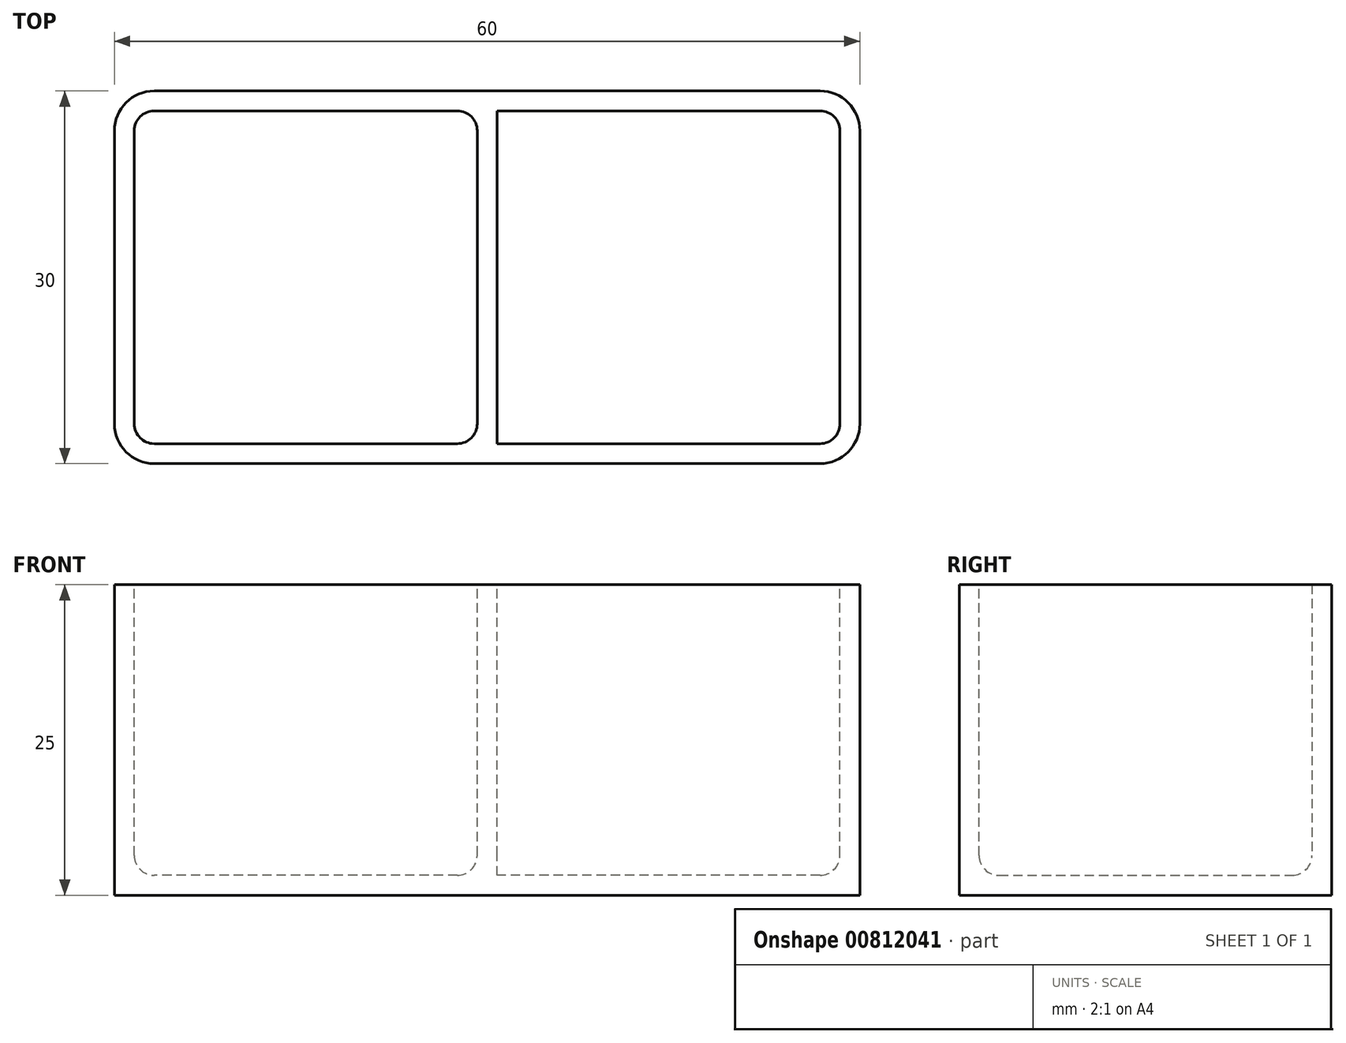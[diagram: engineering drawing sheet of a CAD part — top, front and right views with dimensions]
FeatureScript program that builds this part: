
annotation { "Feature Type Name" : "Feature", "Feature Type Description" : "" }
export const myFeature = defineFeature(function(context is Context, id is Id, definition is map)
    precondition{}
    {
        {
            var Q0;
            Q0=qCreatedBy(makeId("Top.planeOp"),FACE);
            var sketch = newSketch(context, id + "F0", { "sketchPlane" : qUnion([Q0])});
            skLineSegment(sketch, "E0.bottom", {"start": v(30, -15) * mm, "end": v(-30, -15) * mm});
            skLineSegment(sketch, "E0.top", {"start": v(30, 15) * mm, "end": v(-30, 15) * mm});
            skLineSegment(sketch, "E0.left", {"start": v(30, -15) * mm, "end": v(30, 15) * mm});
            skLineSegment(sketch, "E0.right", {"start": v(-30, -15) * mm, "end": v(-30, 15) * mm});
            skPoint(sketch, "E0.middle", {"position": v(0, 0) * mm});
            skSolve(sketch);
        }
        {
            var Q0;
            Q0=makeQuery(id+"F0.imprint","IMPRINT",FACE,{"disambiguationData":[TD([[makeQuery(id+"F0.imprint","IMPRINT",EDGE,{"derivedFrom":sQuery(id+"F0.wireOp",EDGE,"E0.bottom")}),-1.0]])]});
            extrude(context, id + "F1", {"entities" : qUnion([Q0]), "depth" : 25 * mm, "offsetDistance" : 25 * mm});
        }
        {
            var Q0;
            Q0=makeQuery(id+"F1.opExtrude","SWEPT_EDGE",EDGE,{"disambiguationData":[OSD([sQuery(id+"F0.wireOp",EDGE,"E0.top"),sQuery(id+"F0.wireOp",EDGE,"E0.right")])]});
            var Q1;
            Q1=makeQuery(id+"F1.opExtrude","SWEPT_EDGE",EDGE,{"disambiguationData":[OSD([sQuery(id+"F0.wireOp",EDGE,"E0.bottom"),sQuery(id+"F0.wireOp",EDGE,"E0.right")])]});
            var Q2;
            Q2=makeQuery(id+"F1.opExtrude","SWEPT_EDGE",EDGE,{"disambiguationData":[OSD([sQuery(id+"F0.wireOp",EDGE,"E0.bottom"),sQuery(id+"F0.wireOp",EDGE,"E0.left")])]});
            var Q3;
            Q3=makeQuery(id+"F1.opExtrude","SWEPT_EDGE",EDGE,{"disambiguationData":[OSD([sQuery(id+"F0.wireOp",EDGE,"E0.top"),sQuery(id+"F0.wireOp",EDGE,"E0.left")])]});
            fillet(context, id + "F2", {"entities" : qUnion([Q0, Q1, Q2, Q3]), "radius" : 3.2 * mm, "tangentPropagation" : true, "allowEdgeOverflow" : false});
        }
        {
            var Q0;
            Q0=makeQuery(id+"F1.opExtrude","CAP_FACE",FACE,{"disambiguationData":[OSD([sQuery(id+"F0.wireOp",EDGE,"E0.bottom"),sQuery(id+"F0.wireOp",EDGE,"E0.top"),sQuery(id+"F0.wireOp",EDGE,"E0.left"),sQuery(id+"F0.wireOp",EDGE,"E0.right")])],"isStart":false});
            shell(context, id + "F3", {"entities" : qUnion([Q0]), "thickness" : 1.6 * mm});
        }
        {
            var Q0;
            Q0=makeQuery(id+"F1.opExtrude","CAP_FACE",FACE,{"disambiguationData":[OSD([sQuery(id+"F0.wireOp",EDGE,"E0.bottom"),sQuery(id+"F0.wireOp",EDGE,"E0.top"),sQuery(id+"F0.wireOp",EDGE,"E0.left"),sQuery(id+"F0.wireOp",EDGE,"E0.right")])],"isStart":false});
            var sketch = newSketch(context, id + "F4", { "sketchPlane" : qUnion([Q0])});
            skLineSegment(sketch, "E1.0", {"start": v(26.8, 13.4) * mm, "end": v(-26.8, 13.4) * mm});
            skLineSegment(sketch, "E1.1", {"start": v(26.8, -13.4) * mm, "end": v(-26.8, -13.4) * mm});
            skLineSegment(sketch, "E2", {"start": v(0.8, 13.4) * mm, "end": v(0.8, -13.4) * mm});
            skLineSegment(sketch, "E3.MirrorCS", {"start": v(-0.8, 13.4) * mm, "end": v(-0.8, -13.4) * mm});
            skSolve(sketch);
        }
        {
            var Q0;
            {var subQ0=sQuery(id+"F4.wireOp",EDGE,"E2");Q0=makeQuery(id+"F4.imprint","IMPRINT",FACE,{"disambiguationData":[TD([[makeQuery(id+"F4.imprint","IMPRINT",EDGE,{"derivedFrom":subQ0}),-1.0]])]});}
            extrude(context, id + "F5", {"entities" : qUnion([Q0]), "operationType" : NewBodyOperationType.ADD, "endBound" : BoundingType.UP_TO_NEXT, "oppositeDirection" : true, "depth" : 25 * mm, "offsetDistance" : 25 * mm});
        }
        {
            var Q0;
            Q0=makeQuery(id+"F5.opExtrude","SWEPT_EDGE",EDGE,{"disambiguationData":[OSD([sQuery(id+"F4.wireOp",EDGE,"E1.0"),sQuery(id+"F4.wireOp",EDGE,"E3.MirrorCS")])]});
            var Q1;
            Q1=makeQuery(id+"F5.opExtrude","SWEPT_EDGE",EDGE,{"disambiguationData":[OSD([sQuery(id+"F4.wireOp",EDGE,"E1.0"),sQuery(id+"F4.wireOp",EDGE,"E2")])]});
            var Q2;
            Q2=makeQuery(id+"F5.opExtrude","SWEPT_EDGE",EDGE,{"disambiguationData":[OSD([sQuery(id+"F4.wireOp",EDGE,"E1.1"),sQuery(id+"F4.wireOp",EDGE,"E3.MirrorCS")])]});
            var Q3;
            Q3=makeQuery(id+"F5.opExtrude","SWEPT_EDGE",EDGE,{"disambiguationData":[OSD([sQuery(id+"F4.wireOp",EDGE,"E1.1"),sQuery(id+"F4.wireOp",EDGE,"E2")])]});
            fillet(context, id + "F6", {"entities" : qUnion([Q0, Q1, Q2, Q3]), "radius" : 1.6 * mm, "tangentPropagation" : true, "allowEdgeOverflow" : false});
        }
        {
            var Q0;
            {var subQ1=sQuery(id+"F0.wireOp",EDGE,"E0.top");Q0=makeQuery(id+"F5.boolean.opBoolean","SPLIT",EDGE,{"disambiguationData":[TD([makeQuery(id+"F5.opExtrude","SWEPT_FACE",FACE,{"disambiguationData":[OSD([sQuery(id+"F4.wireOp",EDGE,"E3.MirrorCS")])]})])],"derivedFrom":makeQuery(id+"F3.opShell","OFFSET_EDGE",EDGE,{"disambiguationData":[OSD([subQ1]),TDD([makeQuery(id+"F1.opExtrude","CAP_EDGE",EDGE,{"disambiguationData":[OSD([subQ1])],"isStart":true})])]})});}
            var Q1;
            {var subQ1=sQuery(id+"F0.wireOp",EDGE,"E0.top");Q1=makeQuery(id+"F5.boolean.opBoolean","SPLIT",EDGE,{"disambiguationData":[TD([makeQuery(id+"F5.opExtrude","SWEPT_FACE",FACE,{"disambiguationData":[OSD([sQuery(id+"F4.wireOp",EDGE,"E2")])]})])],"derivedFrom":makeQuery(id+"F3.opShell","OFFSET_EDGE",EDGE,{"disambiguationData":[OSD([subQ1]),TDD([makeQuery(id+"F1.opExtrude","CAP_EDGE",EDGE,{"disambiguationData":[OSD([subQ1])],"isStart":true})])]})});}
            fillet(context, id + "F7", {"entities" : qUnion([Q0, Q1]), "radius" : 1.6 * mm, "tangentPropagation" : true, "allowEdgeOverflow" : false});
        }
    });
